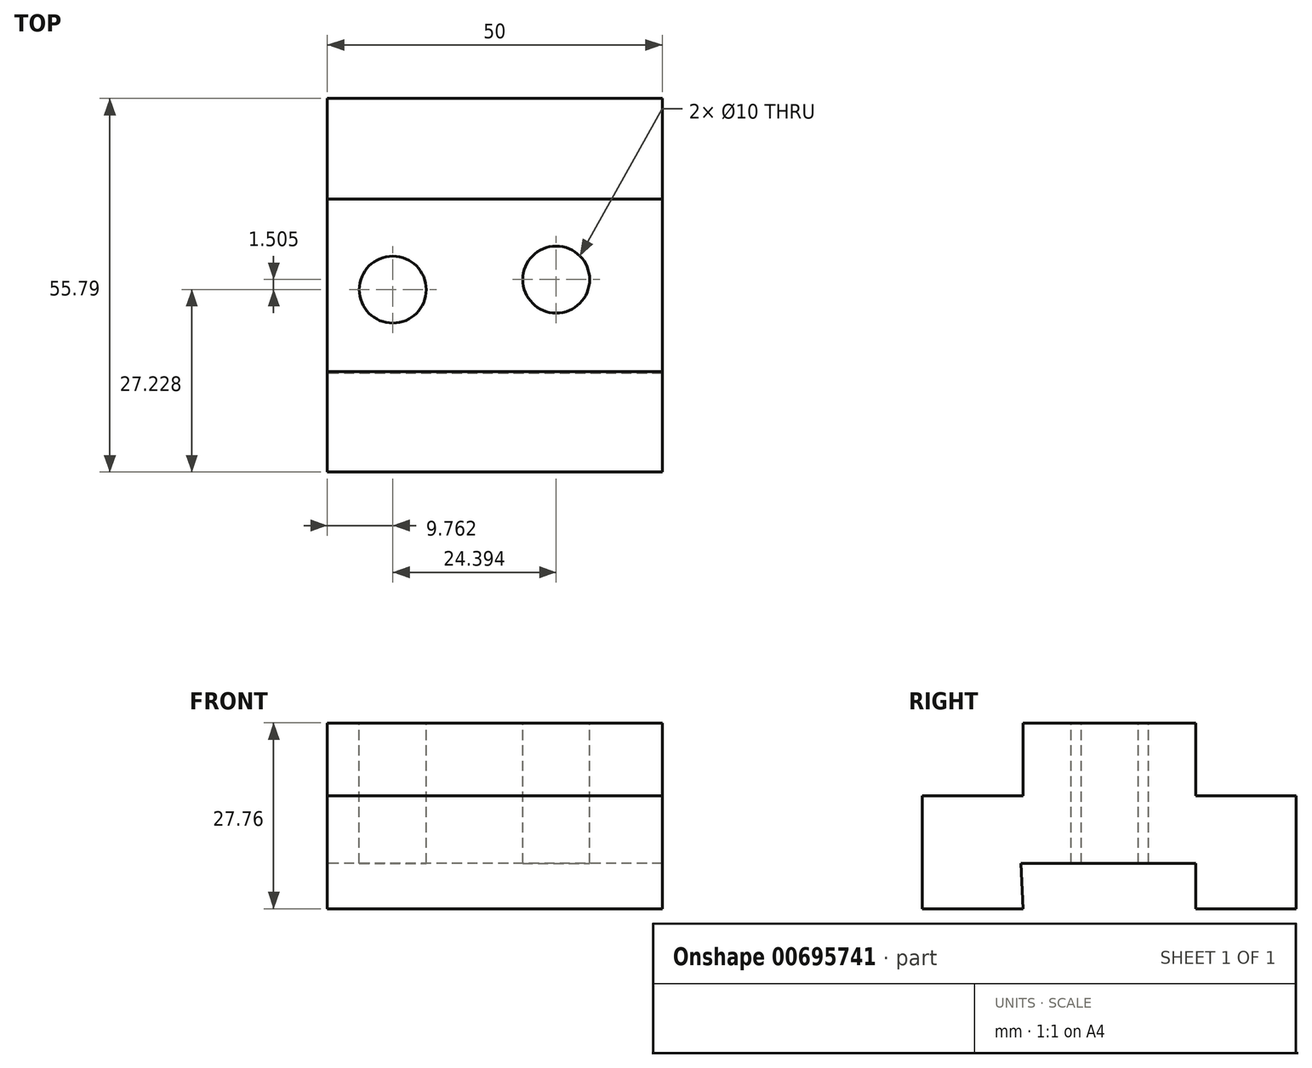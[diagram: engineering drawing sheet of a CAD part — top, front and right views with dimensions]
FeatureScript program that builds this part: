
annotation { "Feature Type Name" : "Feature", "Feature Type Description" : "" }
export const myFeature = defineFeature(function(context is Context, id is Id, definition is map)
    precondition{}
    {
        {
            var Q0;
            Q0=qCreatedBy(makeId("Right.planeOp"),FACE);
            var sketch = newSketch(context, id + "F0", { "sketchPlane" : qUnion([Q0])});
            skLineSegment(sketch, "E0", {"start": v(-62.74, -16.85) * mm, "end": v(-47.74, -16.85) * mm});
            skLineSegment(sketch, "E1", {"start": v(-62.74, -16.85) * mm, "end": v(-62.74, 0) * mm});
            skLineSegment(sketch, "E2", {"start": v(-62.74, 0) * mm, "end": v(-47.74, 0) * mm});
            skLineSegment(sketch, "E3", {"start": v(-47.74, 0) * mm, "end": v(-47.74, 10.9) * mm});
            skLineSegment(sketch, "E4", {"start": v(-47.74, 10.9) * mm, "end": v(-21.95, 10.9) * mm});
            skLineSegment(sketch, "E5", {"start": v(-21.95, 10.9) * mm, "end": v(-21.95, 0) * mm});
            skLineSegment(sketch, "E6", {"start": v(-21.95, 0) * mm, "end": v(-6.95, 0) * mm});
            skLineSegment(sketch, "E7", {"start": v(-6.95, 0) * mm, "end": v(-6.95, -16.86) * mm});
            skLineSegment(sketch, "E8", {"start": v(-6.95, -16.86) * mm, "end": v(-21.95, -16.86) * mm});
            skLineSegment(sketch, "E9", {"start": v(-21.95, -16.86) * mm, "end": v(-21.95, -10.06) * mm});
            skLineSegment(sketch, "E10", {"start": v(-21.95, -10.06) * mm, "end": v(-48.01, -10.06) * mm});
            skLineSegment(sketch, "E11", {"start": v(-48.01, -10.06) * mm, "end": v(-47.74, -16.85) * mm});
            skSolve(sketch);
        }
        {
            var Q0;
            Q0 = qSketchRegion(id + "F0", true);
            extrude(context, id + "F1", {"entities" : qUnion([Q0]), "depth" : 50 * mm, "offsetDistance" : 25 * mm});
        }
        {
            var Q0;
            Q0=makeQuery(id+"F1.opExtrude","SWEPT_FACE",FACE,{"disambiguationData":[OSD([sQuery(id+"F0.wireOp",EDGE,"E4")])]});
            var sketch = newSketch(context, id + "F2", { "sketchPlane" : qUnion([Q0])});
            skCircle(sketch, "E12", {"center": v(9.76, -35.51) * mm, "radius": 5 * mm});
            skCircle(sketch, "E13", {"center": v(34.16, -34) * mm, "radius": 5 * mm});
            skSolve(sketch);
        }
        {
            var Q0;
            Q0 = qSketchRegion(id + "F2", true);
            extrude(context, id + "F3", {"entities" : qUnion([Q0]), "operationType" : NewBodyOperationType.REMOVE, "oppositeDirection" : true, "depth" : 25 * mm, "offsetDistance" : 25 * mm});
        }
    });
